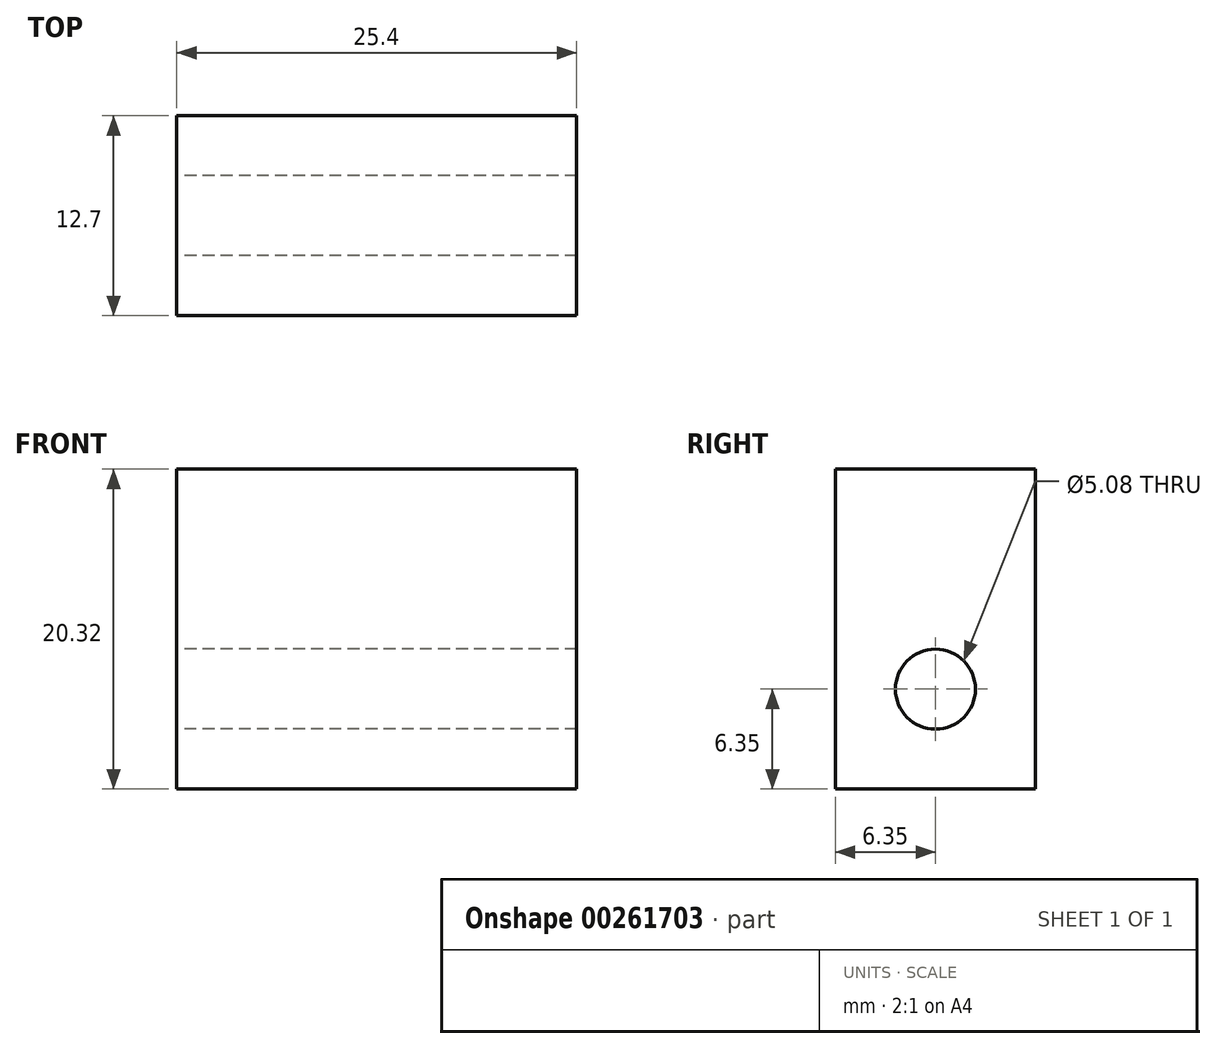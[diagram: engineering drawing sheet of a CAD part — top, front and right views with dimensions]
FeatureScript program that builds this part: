
annotation { "Feature Type Name" : "Feature", "Feature Type Description" : "" }
export const myFeature = defineFeature(function(context is Context, id is Id, definition is map)
    precondition{}
    {
        {
            var Q0;
            Q0=qCreatedBy(makeId("Right.planeOp"),FACE);
            var sketch = newSketch(context, id + "F0", { "sketchPlane" : qUnion([Q0])});
            skLineSegment(sketch, "E0.bottom", {"start": v(0, 0) * mm, "end": v(-12.7, 0) * mm});
            skLineSegment(sketch, "E0.top", {"start": v(0, -20.32) * mm, "end": v(-12.7, -20.32) * mm});
            skLineSegment(sketch, "E0.left", {"start": v(0, 0) * mm, "end": v(0, -20.32) * mm});
            skLineSegment(sketch, "E0.right", {"start": v(-12.7, 0) * mm, "end": v(-12.7, -20.32) * mm});
            skLineSegment(sketch, "E1", {"start": v(-6.35, 0) * mm, "end": v(-6.35, -20.32) * mm});
            skLineSegment(sketch, "E2", {"start": v(0, -13.97) * mm, "end": v(-12.7, -13.97) * mm});
            skCircle(sketch, "E3", {"center": v(-6.35, -13.97) * mm, "radius": 2.54 * mm});
            skSolve(sketch);
        }
        {
            var Q0;
            {var subQ1=sQuery(id+"F0.wireOp",EDGE,"E0.left");var subQ6=sQuery(id+"F0.wireOp",EDGE,"E0.bottom");var subQ9=makeQuery(id+"F0.imprint","INTERSECT",VERTEX,{"derivedFrom":[subQ6,subQ1]});Q0=makeQuery(id+"F0.imprint","IMPRINT",FACE,{"disambiguationData":[TD([[makeQuery(id+"F0.imprint","IMPRINT",EDGE,{"disambiguationData":[TD([[subQ9,-1.0]])],"derivedFrom":subQ6}),1.0]])]});}
            var Q1;
            {var subQ1=sQuery(id+"F0.wireOp",EDGE,"E0.right");var subQ6=sQuery(id+"F0.wireOp",EDGE,"E0.bottom");var subQ9=makeQuery(id+"F0.imprint","INTERSECT",VERTEX,{"derivedFrom":[subQ6,subQ1]});Q1=makeQuery(id+"F0.imprint","IMPRINT",FACE,{"disambiguationData":[TD([[makeQuery(id+"F0.imprint","IMPRINT",EDGE,{"disambiguationData":[TD([[subQ9,1.0]])],"derivedFrom":subQ6}),1.0]])]});}
            var Q2;
            {var subQ1=sQuery(id+"F0.wireOp",EDGE,"E0.right");var subQ6=sQuery(id+"F0.wireOp",EDGE,"E0.top");var subQ9=makeQuery(id+"F0.imprint","INTERSECT",VERTEX,{"derivedFrom":[subQ6,subQ1]});Q2=makeQuery(id+"F0.imprint","IMPRINT",FACE,{"disambiguationData":[TD([[makeQuery(id+"F0.imprint","IMPRINT",EDGE,{"disambiguationData":[TD([[subQ9,1.0]])],"derivedFrom":subQ6}),-1.0]])]});}
            var Q3;
            {var subQ1=sQuery(id+"F0.wireOp",EDGE,"E0.top");var subQ5=sQuery(id+"F0.wireOp",EDGE,"E0.left");var subQ6=makeQuery(id+"F0.imprint","INTERSECT",VERTEX,{"derivedFrom":[subQ1,subQ5]});Q3=makeQuery(id+"F0.imprint","IMPRINT",FACE,{"disambiguationData":[TD([[makeQuery(id+"F0.imprint","IMPRINT",EDGE,{"disambiguationData":[TD([[subQ6,-1.0]])],"derivedFrom":subQ1}),-1.0]])]});}
            extrude(context, id + "F1", {"entities" : qUnion([Q0, Q1, Q2, Q3]), "depth" : 25.4 * mm});
        }
    });
